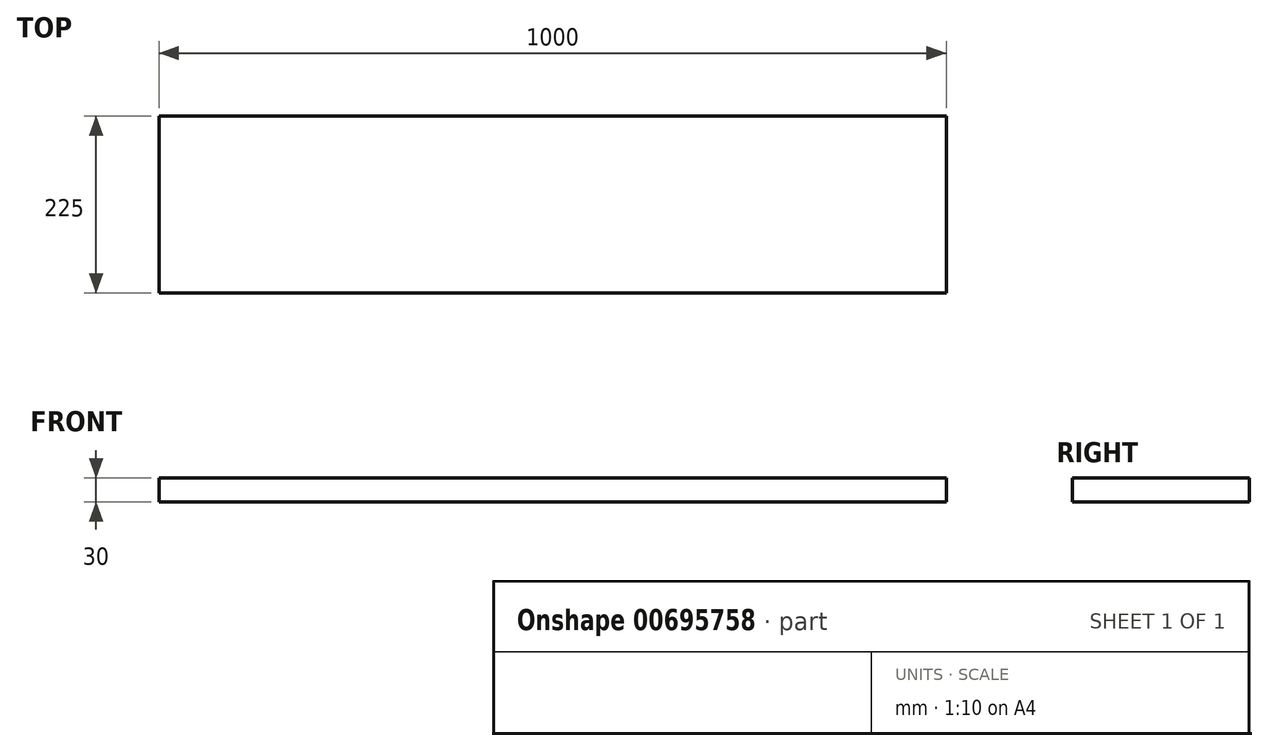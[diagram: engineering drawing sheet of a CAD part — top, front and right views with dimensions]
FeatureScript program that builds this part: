
annotation { "Feature Type Name" : "Feature", "Feature Type Description" : "" }
export const myFeature = defineFeature(function(context is Context, id is Id, definition is map)
    precondition{}
    {
        {
            var Q0;
            Q0=qCreatedBy(makeId("Top.planeOp"),FACE);
            var sketch = newSketch(context, id + "F0", { "sketchPlane" : qUnion([Q0])});
            skLineSegment(sketch, "E0.bottom", {"start": v(-503.6, -214.07) * mm, "end": v(496.4, -214.07) * mm});
            skLineSegment(sketch, "E0.top", {"start": v(-503.6, 10.93) * mm, "end": v(496.4, 10.93) * mm});
            skLineSegment(sketch, "E0.left", {"start": v(-503.6, -214.07) * mm, "end": v(-503.6, 10.93) * mm});
            skLineSegment(sketch, "E0.right", {"start": v(496.4, -214.07) * mm, "end": v(496.4, 10.93) * mm});
            skSolve(sketch);
        }
        {
            var Q0;
            Q0=makeQuery(id+"F0.imprint","IMPRINT",FACE,{"disambiguationData":[TD([[makeQuery(id+"F0.imprint","IMPRINT",EDGE,{"derivedFrom":sQuery(id+"F0.wireOp",EDGE,"E0.bottom")}),1.0]])]});
            extrude(context, id + "F1", {"entities" : qUnion([Q0]), "depth" : 30 * mm, "offsetDistance" : 25 * mm});
        }
    });
